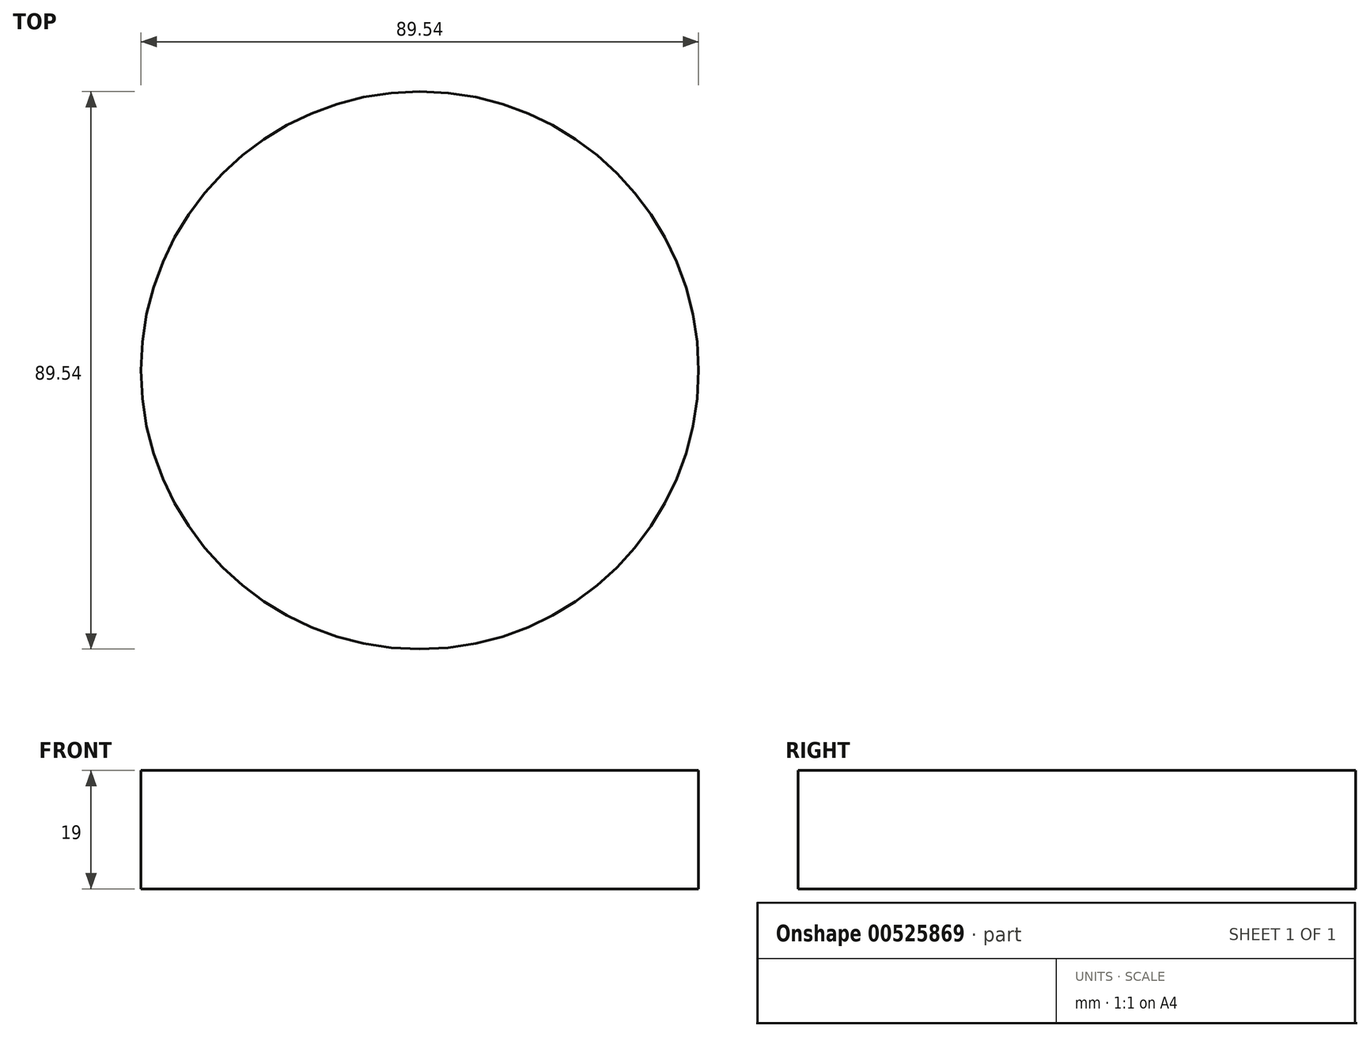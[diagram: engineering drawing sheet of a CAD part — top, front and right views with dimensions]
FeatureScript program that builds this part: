
annotation { "Feature Type Name" : "Feature", "Feature Type Description" : "" }
export const myFeature = defineFeature(function(context is Context, id is Id, definition is map)
    precondition{}
    {
        {
            var Q0;
            Q0=qCreatedBy(makeId("Top.planeOp"),FACE);
            var sketch = newSketch(context, id + "F0", { "sketchPlane" : qUnion([Q0])});
            skCircle(sketch, "E0", {"center": v(0, 0) * mm, "radius": 44.77 * mm});
            skSolve(sketch);
        }
        {
            var Q0;
            Q0=makeQuery(id+"F0.imprint","IMPRINT",FACE,{"disambiguationData":[TD([[makeQuery(id+"F0.imprint","IMPRINT",EDGE,{"derivedFrom":sQuery(id+"F0.wireOp",EDGE,"E0")}),1.0]])]});
            extrude(context, id + "F1", {"entities" : qUnion([Q0]), "depth" : 19 * mm, "offsetDistance" : 25 * mm});
        }
    });
